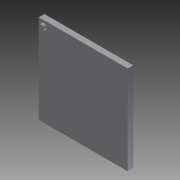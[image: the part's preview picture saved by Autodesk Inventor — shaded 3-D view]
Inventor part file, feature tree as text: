
AUTODESK INVENTOR PART (.ipt)
format: ipt  version: 2011 (Build 150239000, 239)  size: 105,472 bytes
history: native  units: in
note: dims shown in document units (in); Inventor stores cm internally (conversion verified against a paired STEP export)
features: extrude x6, sketch x6
ambient origin geometry x8: Origin, YZ Plane, XZ Plane, XY Plane, X Axis, Y Axis, Z Axis, Center Point
bodies: Solid1 (feature_tree)
feature tree (12):
  extrude  "Extrusion1"  Depth=4.0in
  extrude  "Extrusion2"  Depth=2.0in
  extrude  "Extrusion3"  Depth=1.0in
  extrude  "Extrusion4"  Depth=2.0in
  extrude  "Extrusion5"  Depth=0.435in
  extrude  "Extrusion6"  Depth=0.25in TaperAngle=0.0deg
  sketch  "Sketch1"  dims[d0=4.0in d1=4.0in]
  sketch  "Sketch2"  dims[d2=0.25in d3=0.0in d4=2.0in]
  sketch  "Sketch3"  dims[d5=2.0in d6=1.0in]
  sketch  "Sketch4"  dims[d7=0.25in d8=0.0in d9=2.0in]
  sketch  "Sketch5"  dims[d10=1.5655in d11=0.435in]
  sketch  "Sketch6"  dims[d12=0.25in d13=0.25in d14=0.0in d15=0.75in d16=0.0in d17=2.0in d18=1.7655in d19=0.235in d20=0.25in d21=0.125in d22=0.0in d23=0.25in d24=0.0in]
